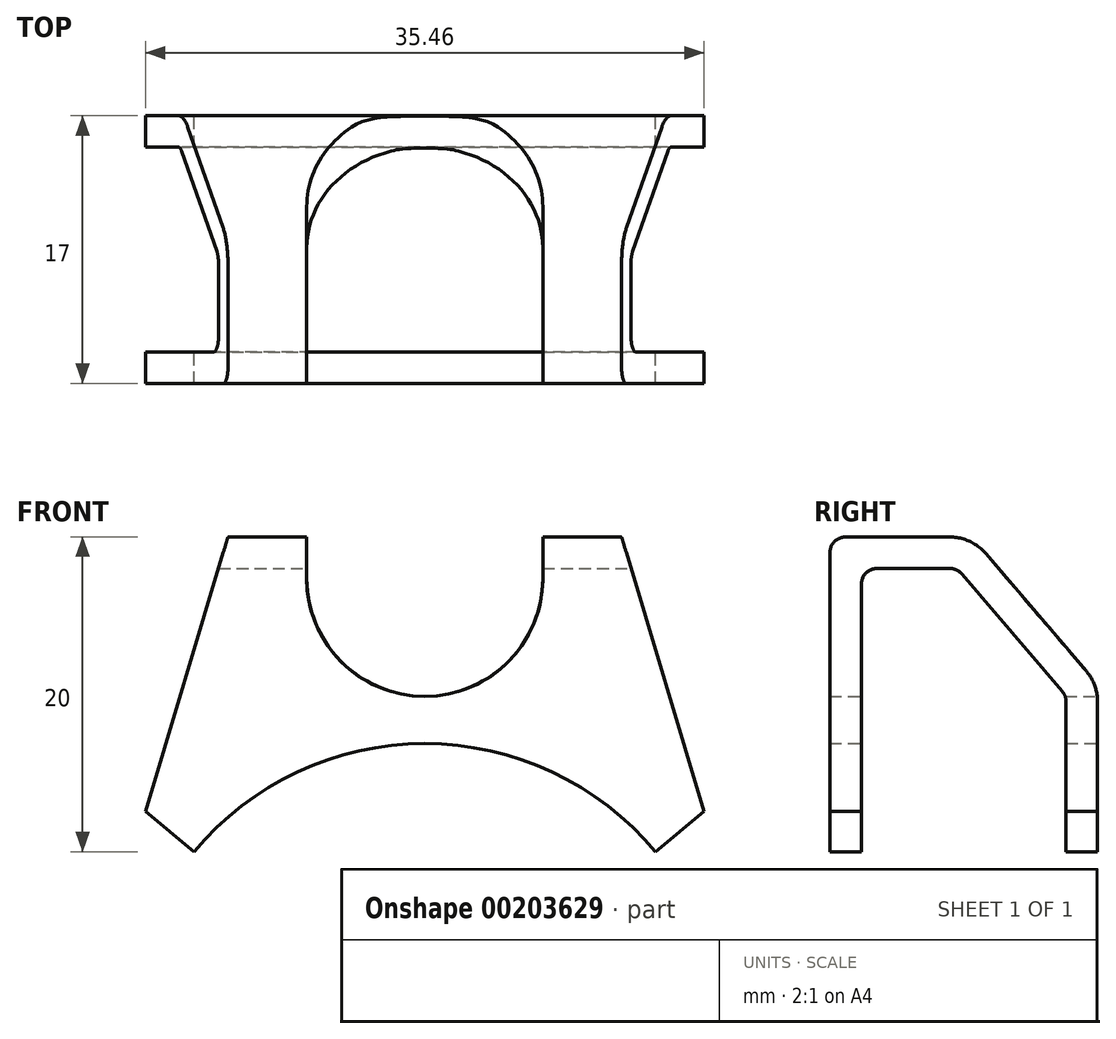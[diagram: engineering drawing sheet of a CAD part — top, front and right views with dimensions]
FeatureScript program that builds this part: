
annotation { "Feature Type Name" : "Feature", "Feature Type Description" : "" }
export const myFeature = defineFeature(function(context is Context, id is Id, definition is map)
    precondition{}
    {
        {
            var Q0;
            Q0=qCreatedBy(makeId("Front.planeOp"),FACE);
            var sketch = newSketch(context, id + "F0", { "sketchPlane" : qUnion([Q0])});
            skCircle(sketch, "E0", {"center": v(0, 0) * mm, "radius": 19.05 * mm});
            skLineSegment(sketch, "E1.bottom", {"start": v(-14.65, 12.18) * mm, "end": v(14.65, 12.18) * mm});
            skLineSegment(sketch, "E1.top", {"start": v(-14.65, 32.18) * mm, "end": v(14.65, 32.18) * mm});
            skLineSegment(sketch, "E1.left", {"start": v(-14.65, 12.18) * mm, "end": v(-14.65, 32.18) * mm});
            skLineSegment(sketch, "E1.right", {"start": v(14.65, 12.18) * mm, "end": v(14.65, 32.18) * mm});
            skLineSegment(sketch, "E2.bottom", {"start": v(-7.5, 32.18) * mm, "end": v(7.5, 32.18) * mm});
            skLineSegment(sketch, "E2.top", {"start": v(-7.5, 29.55) * mm, "end": v(7.5, 29.55) * mm});
            skLineSegment(sketch, "E2.left", {"start": v(-7.5, 32.18) * mm, "end": v(-7.5, 29.55) * mm});
            skLineSegment(sketch, "E2.right", {"start": v(7.5, 32.18) * mm, "end": v(7.5, 29.55) * mm});
            skArc(sketch, "E3", {"start": v(-7.5, 29.55) * mm, "mid": v(0, 22.05) * mm, "end": v(7.5, 29.55) * mm});
            skLineSegment(sketch, "E4", {"start": v(12.5, 32.18) * mm, "end": v(17.73, 14.73) * mm});
            skLineSegment(sketch, "E5", {"start": v(17.73, 14.73) * mm, "end": v(14.65, 12.18) * mm});
            skLineSegment(sketch, "E6", {"start": v(-14.65, 12.18) * mm, "end": v(-17.73, 14.73) * mm});
            skLineSegment(sketch, "E7", {"start": v(-17.73, 14.73) * mm, "end": v(-12.5, 32.18) * mm});
            skSolve(sketch);
        }
        {
            var Q0;
            {var subQ13=sQuery(id+"F0.wireOp",EDGE,"E2.left");Q0=makeQuery(id+"F0.imprint","IMPRINT",FACE,{"disambiguationData":[TD([[makeQuery(id+"F0.imprint","IMPRINT",EDGE,{"derivedFrom":subQ13}),-1.0]])]});}
            var Q1;
            {var subQ0=sQuery(id+"F0.wireOp",EDGE,"E6");Q1=makeQuery(id+"F0.imprint","IMPRINT",FACE,{"disambiguationData":[TD([[makeQuery(id+"F0.imprint","IMPRINT",EDGE,{"derivedFrom":subQ0}),-1.0]])]});}
            var Q2;
            {var subQ0=sQuery(id+"F0.wireOp",EDGE,"E5");Q2=makeQuery(id+"F0.imprint","IMPRINT",FACE,{"disambiguationData":[TD([[makeQuery(id+"F0.imprint","IMPRINT",EDGE,{"derivedFrom":subQ0}),-1.0]])]});}
            extrude(context, id + "F1", {"entities" : qUnion([Q0, Q1, Q2]), "depth" : 17 * mm});
        }
        {
            var Q0;
            Q0=qCreatedBy(makeId("Right.planeOp"),FACE);
            var sketch = newSketch(context, id + "F2", { "sketchPlane" : qUnion([Q0])});
            skLineSegment(sketch, "E8.0", {"start": v(-17, 31.18) * mm, "end": v(-17, 14.73) * mm});
            skLineSegment(sketch, "E9.0", {"start": v(-17, 14.73) * mm, "end": v(-17, 12.18) * mm});
            skLineSegment(sketch, "E10.0", {"start": v(-16, 32.18) * mm, "end": v(-9.38, 32.18) * mm});
            skPoint(sketch, "E11.visualSharp", {"position": v(-17, 32.18) * mm});
            skArc(sketch, "E11.filletArc", {"start": v(-16, 32.18) * mm, "mid": v(-16.7, 31.88) * mm, "end": v(-17, 31.18) * mm});
            skLineSegment(sketch, "E12", {"start": v(-7.1, 31.13) * mm, "end": v(-0.72, 23.66) * mm});
            skLineSegment(sketch, "E13.0", {"start": v(0, 14.73) * mm, "end": v(0, 12.18) * mm});
            skLineSegment(sketch, "E14.0", {"start": v(0, 21.71) * mm, "end": v(0, 14.73) * mm});
            skPoint(sketch, "E15.newPointA", {"position": v(0, 32.18) * mm});
            skPoint(sketch, "E15.newPointB", {"position": v(-8, 32.18) * mm});
            skArc(sketch, "E15.filletArc", {"start": v(-7.1, 31.13) * mm, "mid": v(-8.13, 31.9) * mm, "end": v(-9.38, 32.18) * mm});
            skPoint(sketch, "E16.newPointB", {"position": v(0, 22.82) * mm});
            skArc(sketch, "E16.filletArc", {"start": v(0, 21.71) * mm, "mid": v(-0.19, 22.75) * mm, "end": v(-0.72, 23.66) * mm});
            skLineSegment(sketch, "E17.0", {"start": v(-15, 14.73) * mm, "end": v(-15, 12.18) * mm});
            skLineSegment(sketch, "E17.1", {"start": v(-15, 29.18) * mm, "end": v(-15, 14.73) * mm});
            skLineSegment(sketch, "E17.2", {"start": v(-14, 30.18) * mm, "end": v(-9.38, 30.18) * mm});
            skArc(sketch, "E17.3", {"start": v(-8.62, 29.83) * mm, "mid": v(-8.96, 30.09) * mm, "end": v(-9.38, 30.18) * mm});
            skLineSegment(sketch, "E17.4", {"start": v(-2, 14.73) * mm, "end": v(-2, 12.18) * mm});
            skLineSegment(sketch, "E17.5", {"start": v(-2, 21.71) * mm, "end": v(-2, 14.73) * mm});
            skArc(sketch, "E17.6", {"start": v(-2, 21.71) * mm, "mid": v(-2.06, 22.06) * mm, "end": v(-2.24, 22.36) * mm});
            skLineSegment(sketch, "E17.7", {"start": v(-8.62, 29.83) * mm, "end": v(-2.24, 22.36) * mm});
            skPoint(sketch, "E18.visualSharp", {"position": v(-15, 30.18) * mm});
            skArc(sketch, "E18.filletArc", {"start": v(-14, 30.18) * mm, "mid": v(-14.7, 29.88) * mm, "end": v(-15, 29.18) * mm});
            skLineSegment(sketch, "E19", {"start": v(-17, 12.18) * mm, "end": v(-15, 12.18) * mm});
            skLineSegment(sketch, "E20", {"start": v(-2, 12.18) * mm, "end": v(0, 12.18) * mm});
            skLineSegment(sketch, "E21", {"start": v(-15, 12.18) * mm, "end": v(-2, 12.18) * mm});
            skLineSegment(sketch, "E22", {"start": v(0, 21.71) * mm, "end": v(0, 32.18) * mm});
            skLineSegment(sketch, "E23", {"start": v(0, 32.18) * mm, "end": v(-9.38, 32.18) * mm});
            skLineSegment(sketch, "E24", {"start": v(-16, 32.18) * mm, "end": v(-17, 32.18) * mm});
            skLineSegment(sketch, "E25", {"start": v(-17, 32.18) * mm, "end": v(-17, 31.18) * mm});
            skSolve(sketch);
        }
        {
            var Q0;
            Q0=makeQuery(id+"F2.imprint","IMPRINT",FACE,{"disambiguationData":[TD([[makeQuery(id+"F2.imprint","IMPRINT",EDGE,{"derivedFrom":sQuery(id+"F2.wireOp",EDGE,"E12")}),1.0]])]});
            var Q1;
            Q1=makeQuery(id+"F2.imprint","IMPRINT",FACE,{"disambiguationData":[TD([[makeQuery(id+"F2.imprint","IMPRINT",EDGE,{"derivedFrom":sQuery(id+"F2.wireOp",EDGE,"E17.0")}),1.0]])]});
            var Q2;
            Q2=makeQuery(id+"F2.imprint","IMPRINT",FACE,{"disambiguationData":[TD([[makeQuery(id+"F2.imprint","IMPRINT",EDGE,{"derivedFrom":sQuery(id+"F2.wireOp",EDGE,"E11.filletArc")}),-1.0]])]});
            extrude(context, id + "F3", {"entities" : qUnion([Q0, Q1, Q2]), "operationType" : NewBodyOperationType.REMOVE, "endBound" : BoundingType.SYMMETRIC, "oppositeDirection" : true, "depth" : 40 * mm});
        }
    });
